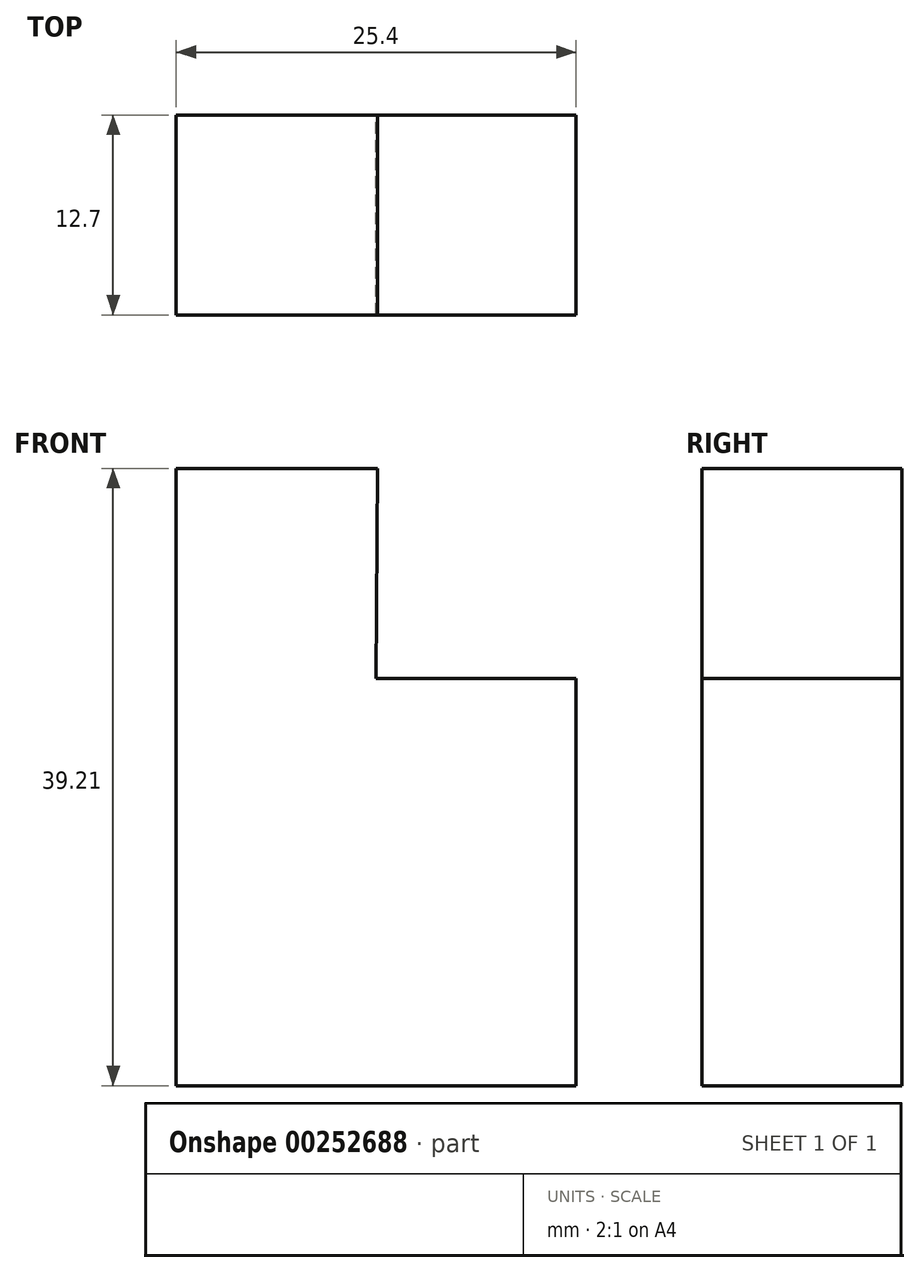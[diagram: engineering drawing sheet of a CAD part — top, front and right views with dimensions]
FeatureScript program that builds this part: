
annotation { "Feature Type Name" : "Feature", "Feature Type Description" : "" }
export const myFeature = defineFeature(function(context is Context, id is Id, definition is map)
    precondition{}
    {
        {
            var Q0;
            Q0=qCreatedBy(makeId("Front.planeOp"),FACE);
            var sketch = newSketch(context, id + "F0", { "sketchPlane" : qUnion([Q0])});
            skLineSegment(sketch, "E0", {"start": v(0, 0) * mm, "end": v(0, 39.21) * mm});
            skLineSegment(sketch, "E1", {"start": v(0, 0) * mm, "end": v(25.4, 0) * mm});
            skLineSegment(sketch, "E2", {"start": v(25.4, 0) * mm, "end": v(25.4, 25.88) * mm});
            skLineSegment(sketch, "E3", {"start": v(25.4, 25.88) * mm, "end": v(12.7, 25.88) * mm});
            skLineSegment(sketch, "E4", {"start": v(0, 39.21) * mm, "end": v(12.8, 39.21) * mm});
            skLineSegment(sketch, "E5", {"start": v(12.8, 39.21) * mm, "end": v(12.7, 25.88) * mm});
            skSolve(sketch);
        }
        {
            var Q0;
            Q0=makeQuery(id+"F0.imprint","IMPRINT",FACE,{"disambiguationData":[TD([[makeQuery(id+"F0.imprint","IMPRINT",EDGE,{"derivedFrom":sQuery(id+"F0.wireOp",EDGE,"E0")}),-1.0]])]});
            extrude(context, id + "F1", {"entities" : qUnion([Q0]), "depth" : 12.7 * mm});
        }
    });
